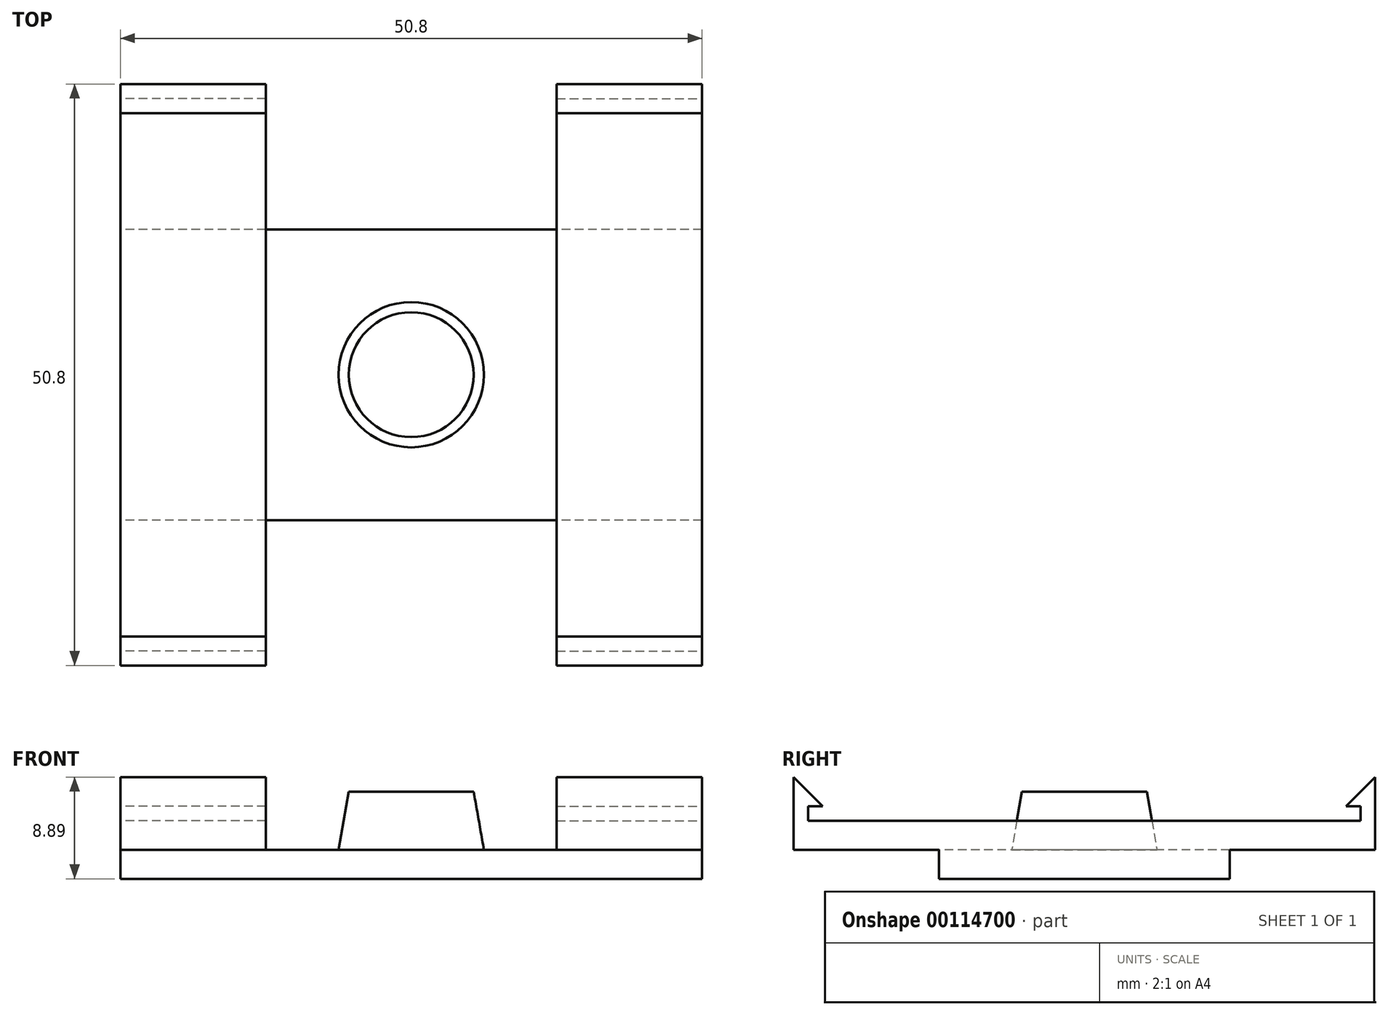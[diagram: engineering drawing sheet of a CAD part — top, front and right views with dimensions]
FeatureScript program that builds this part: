
annotation { "Feature Type Name" : "Feature", "Feature Type Description" : "" }
export const myFeature = defineFeature(function(context is Context, id is Id, definition is map)
    precondition{}
    {
        {
            var Q0;
            Q0=qCreatedBy(makeId("Top.planeOp"),FACE);
            var sketch = newSketch(context, id + "F0", { "sketchPlane" : qUnion([Q0])});
            skLineSegment(sketch, "E0.bottom", {"start": v(25.4, -12.7) * mm, "end": v(-25.4, -12.7) * mm});
            skLineSegment(sketch, "E0.top", {"start": v(25.4, 12.7) * mm, "end": v(-25.4, 12.7) * mm});
            skLineSegment(sketch, "E0.left", {"start": v(25.4, -12.7) * mm, "end": v(25.4, 12.7) * mm});
            skLineSegment(sketch, "E0.right", {"start": v(-25.4, -12.7) * mm, "end": v(-25.4, 12.7) * mm});
            skPoint(sketch, "E0.middle", {"position": v(0, 0) * mm});
            skSolve(sketch);
        }
        {
            var Q0;
            Q0=makeQuery(id+"F0.imprint","IMPRINT",FACE,{"disambiguationData":[TD([[makeQuery(id+"F0.imprint","IMPRINT",EDGE,{"derivedFrom":sQuery(id+"F0.wireOp",EDGE,"E0.bottom")}),-1.0]])]});
            extrude(context, id + "F1", {"entities" : qUnion([Q0]), "depth" : 2.54 * mm});
        }
        {
            var Q0;
            Q0=makeQuery(id+"F1.opExtrude","CAP_FACE",FACE,{"disambiguationData":[OSD([sQuery(id+"F0.wireOp",EDGE,"E0.bottom"),sQuery(id+"F0.wireOp",EDGE,"E0.top"),sQuery(id+"F0.wireOp",EDGE,"E0.left"),sQuery(id+"F0.wireOp",EDGE,"E0.right")])],"isStart":false});
            var sketch = newSketch(context, id + "F2", { "sketchPlane" : qUnion([Q0])});
            skLineSegment(sketch, "E1.bottom", {"start": v(-25.4, 25.4) * mm, "end": v(-12.7, 25.4) * mm});
            skLineSegment(sketch, "E1.top", {"start": v(-25.4, -25.4) * mm, "end": v(-12.7, -25.4) * mm});
            skLineSegment(sketch, "E1.left", {"start": v(-25.4, 25.4) * mm, "end": v(-25.4, -25.4) * mm});
            skLineSegment(sketch, "E1.right", {"start": v(-12.7, 25.4) * mm, "end": v(-12.7, -25.4) * mm});
            skPoint(sketch, "E2", {"position": v(-25.4, 0) * mm});
            skSolve(sketch);
        }
        {
            var Q0;
            Q0 = qSketchRegion(id + "F2", true);
            extrude(context, id + "F3", {"entities" : qUnion([Q0]), "operationType" : NewBodyOperationType.ADD, "depth" : 2.54 * mm});
        }
        {
            var Q0;
            Q0=makeQuery(id+"F3.opExtrude","CAP_FACE",FACE,{"disambiguationData":[OSD([sQuery(id+"F2.wireOp",EDGE,"E1.bottom"),sQuery(id+"F2.wireOp",EDGE,"E1.top"),sQuery(id+"F2.wireOp",EDGE,"E1.left"),sQuery(id+"F2.wireOp",EDGE,"E1.right")])],"isStart":false});
            var sketch = newSketch(context, id + "F4", { "sketchPlane" : qUnion([Q0])});
            skLineSegment(sketch, "E3.bottom", {"start": v(-12.7, 25.4) * mm, "end": v(-25.4, 25.4) * mm});
            skLineSegment(sketch, "E3.top", {"start": v(-12.7, 22.86) * mm, "end": v(-25.4, 22.86) * mm});
            skLineSegment(sketch, "E3.left", {"start": v(-12.7, 25.4) * mm, "end": v(-12.7, 22.86) * mm});
            skLineSegment(sketch, "E3.right", {"start": v(-25.4, 25.4) * mm, "end": v(-25.4, 22.86) * mm});
            skSolve(sketch);
        }
        {
            var Q0;
            Q0 = qSketchRegion(id + "F4", true);
            extrude(context, id + "F5", {"entities" : qUnion([Q0]), "operationType" : NewBodyOperationType.ADD, "depth" : 3.8 * mm});
        }
        {
            var Q0;
            Q0=makeQuery(id+"F5.boolean.opBoolean","MERGE",FACE,{"derivedFrom":[makeQuery(id+"F3.boolean.opBoolean","MERGE",FACE,{"derivedFrom":[makeQuery(id+"F1.opExtrude","SWEPT_FACE",FACE,{"disambiguationData":[OSD([sQuery(id+"F0.wireOp",EDGE,"E0.right")])]}),makeQuery(id+"F3.opExtrude","SWEPT_FACE",FACE,{"disambiguationData":[OSD([sQuery(id+"F2.wireOp",EDGE,"E1.left")])]})]}),makeQuery(id+"F5.opExtrude","SWEPT_FACE",FACE,{"disambiguationData":[OSD([sQuery(id+"F4.wireOp",EDGE,"GXmjIs5c-uSum-NX7N-nHYs-OoZsCVWimQKU.right")])]}),makeQuery(id+"F5.opExtrude","SWEPT_FACE",FACE,{"disambiguationData":[OSD([sQuery(id+"F4.wireOp",EDGE,"E3.right")])]})]});
            var sketch = newSketch(context, id + "F6", { "sketchPlane" : qUnion([Q0])});
            skLineSegment(sketch, "E4", {"start": v(-25.4, 8.9) * mm, "end": v(-22.86, 6.35) * mm});
            skLineSegment(sketch, "E5", {"start": v(-24.13, 8.9) * mm, "end": v(-24.13, 6.35) * mm, "construction": true});
            skLineSegment(sketch, "E6.bottom", {"start": v(-24.13, 6.35) * mm, "end": v(-22.86, 6.35) * mm});
            skLineSegment(sketch, "E6.top", {"start": v(-24.13, 5.08) * mm, "end": v(-22.86, 5.08) * mm});
            skLineSegment(sketch, "E6.left", {"start": v(-24.13, 6.35) * mm, "end": v(-24.13, 5.08) * mm});
            skLineSegment(sketch, "E6.right", {"start": v(-22.86, 6.35) * mm, "end": v(-22.86, 5.08) * mm});
            skLineSegment(sketch, "E7", {"start": v(-25.4, 8.9) * mm, "end": v(-22.86, 8.9) * mm});
            skLineSegment(sketch, "E8", {"start": v(-22.86, 8.9) * mm, "end": v(-22.86, 6.35) * mm});
            skSolve(sketch);
        }
        {
            var Q0;
            Q0 = qSketchRegion(id + "F6", true);
            extrude(context, id + "F7", {"entities" : qUnion([Q0]), "operationType" : NewBodyOperationType.REMOVE, "oppositeDirection" : true, "depth" : 25.4 * mm});
        }
        {
            var Q0;
            Q0=makeQuery(id+"F1.opExtrude","SWEPT_BODY",BODY,{"disambiguationData":[OSD([sQuery(id+"F0.wireOp",EDGE,"E0.bottom"),sQuery(id+"F0.wireOp",EDGE,"E0.top"),sQuery(id+"F0.wireOp",EDGE,"E0.left"),sQuery(id+"F0.wireOp",EDGE,"E0.right")])]});
            var Q1;
            Q1=qCreatedBy(makeId("Front.planeOp"),FACE);
            mirror(context, id + "F8", {"entities" : qUnion([Q0]), "mirrorPlane" : qUnion([Q1])});
        }
        {
            var Q0;
            Q0=makeQuery(id+"F1.opExtrude","SWEPT_BODY",BODY,{"disambiguationData":[OSD([sQuery(id+"F0.wireOp",EDGE,"E0.bottom"),sQuery(id+"F0.wireOp",EDGE,"E0.top"),sQuery(id+"F0.wireOp",EDGE,"E0.left"),sQuery(id+"F0.wireOp",EDGE,"E0.right")])]});
            var Q1;
            Q1=makeQuery(id+"F8.opPattern","COPY",BODY,{"derivedFrom":makeQuery(id+"F1.opExtrude","SWEPT_BODY",BODY,{"disambiguationData":[OSD([sQuery(id+"F0.wireOp",EDGE,"E0.bottom"),sQuery(id+"F0.wireOp",EDGE,"E0.top"),sQuery(id+"F0.wireOp",EDGE,"E0.left"),sQuery(id+"F0.wireOp",EDGE,"E0.right")])]}),"instanceName":"1"});
            var Q2;
            Q2=qCreatedBy(makeId("Right.planeOp"),FACE);
            mirror(context, id + "F9", {"entities" : qUnion([Q0, Q1]), "mirrorPlane" : qUnion([Q2])});
        }
        {
            var Q0;
            Q0=makeQuery(id+"F9.opPattern","COPY",FACE,{"derivedFrom":makeQuery(id+"F1.opExtrude","CAP_FACE",FACE,{"disambiguationData":[OSD([sQuery(id+"F0.wireOp",EDGE,"E0.bottom"),sQuery(id+"F0.wireOp",EDGE,"E0.top"),sQuery(id+"F0.wireOp",EDGE,"E0.left"),sQuery(id+"F0.wireOp",EDGE,"E0.right")])],"isStart":false}),"instanceName":"1"});
            var sketch = newSketch(context, id + "F10", { "sketchPlane" : qUnion([Q0])});
            skCircle(sketch, "E9", {"center": v(0, 0) * mm, "radius": 6.35 * mm});
            skSolve(sketch);
        }
        {
            var Q0;
            Q0=makeQuery(id+"F10.imprint","IMPRINT",FACE,{"disambiguationData":[TD([[makeQuery(id+"F10.imprint","IMPRINT",EDGE,{"derivedFrom":sQuery(id+"F10.wireOp",EDGE,"E9")}),1.0]])]});
            extrude(context, id + "F11", {"entities" : qUnion([Q0]), "operationType" : NewBodyOperationType.ADD, "depth" : 5.08 * mm, "hasDraft" : true, "draftAngle" : 10 * degree, "draftPullDirection" : true});
        }
    });
